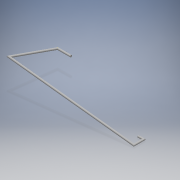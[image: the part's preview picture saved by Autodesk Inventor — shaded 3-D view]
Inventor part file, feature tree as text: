
AUTODESK INVENTOR PART (.ipt)
format: ipt  version: 2017 (Build 210142000, 142)  size: 120,320 bytes
history: native  units: in
note: dims shown in document units (in); Inventor stores cm internally (conversion verified against a paired STEP export)
features: other x4, sketch x2, sweep x1
ambient origin geometry x8: Origin, YZ Plane, XZ Plane, XY Plane, X Axis, Y Axis, Z Axis, Center Point
bodies: Solid1 (feature_tree)
feature tree (7):
  sweep  "Sweep1"
  sketch  "Sketch1"  dims[d0=0.0in d1=0.0in d2=0.0787in d3=0.0787in d4=0.0787in d5=0.0787in d6=0.7in]
  sketch  "3D Sketch1"
  other  "Work Point1"
  other  "<userpath>\Desktop\asa1\assembly.iam"
  other  "assembly.iam"
  other  "capaservo:1"
